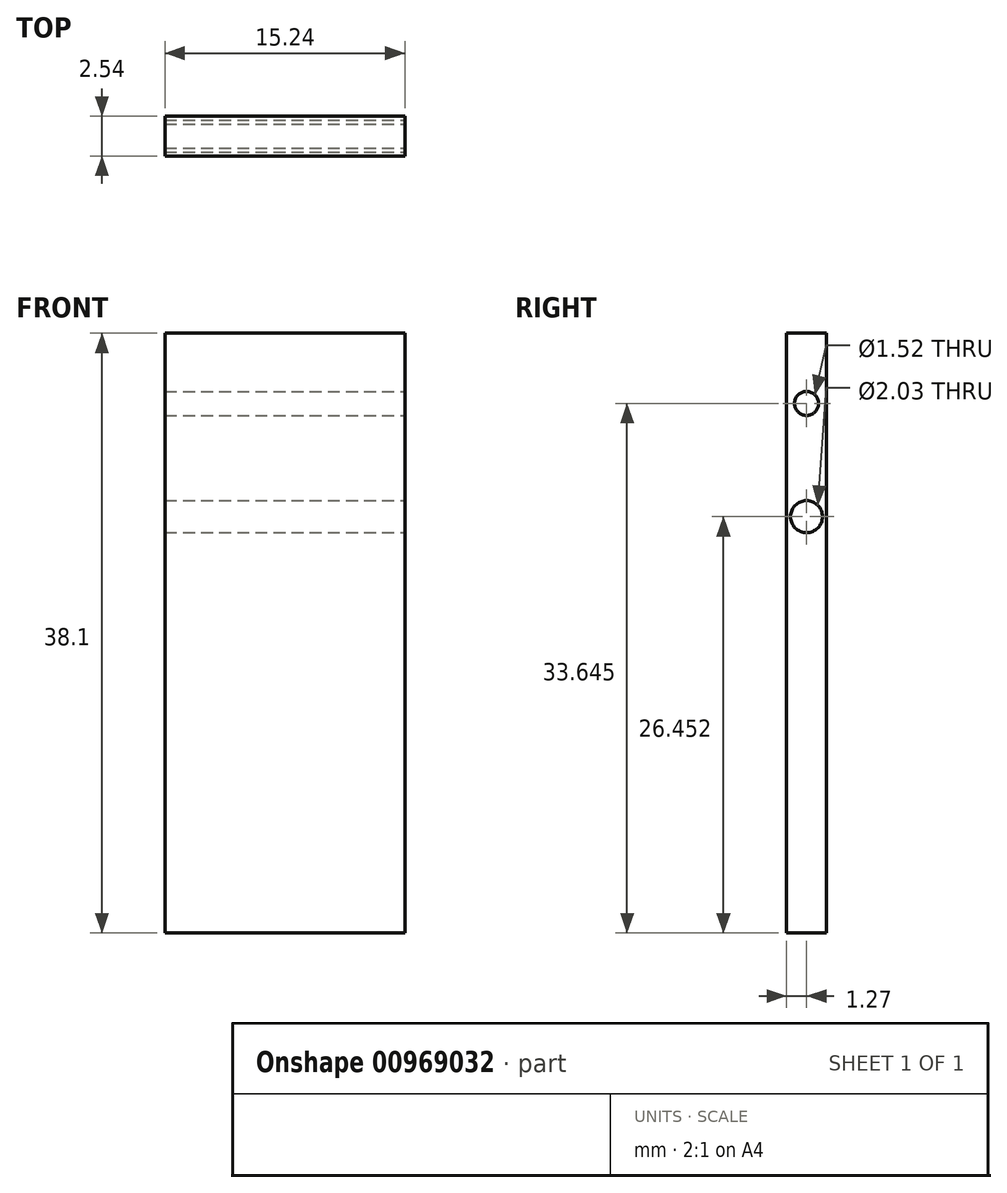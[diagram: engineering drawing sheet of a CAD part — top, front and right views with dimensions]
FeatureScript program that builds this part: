
annotation { "Feature Type Name" : "Feature", "Feature Type Description" : "" }
export const myFeature = defineFeature(function(context is Context, id is Id, definition is map)
    precondition{}
    {
        {
            var Q0;
            Q0=qCreatedBy(makeId("Front.planeOp"),FACE);
            var sketch = newSketch(context, id + "F0", { "sketchPlane" : qUnion([Q0])});
            skLineSegment(sketch, "E0.bottom", {"start": v(7.62, 19.05) * mm, "end": v(-7.62, 19.05) * mm});
            skLineSegment(sketch, "E0.top", {"start": v(7.62, -19.05) * mm, "end": v(-7.62, -19.05) * mm});
            skLineSegment(sketch, "E0.left", {"start": v(7.62, 19.05) * mm, "end": v(7.62, -19.05) * mm});
            skLineSegment(sketch, "E0.right", {"start": v(-7.62, 19.05) * mm, "end": v(-7.62, -19.05) * mm});
            skPoint(sketch, "E0.middle", {"position": v(0, 0) * mm});
            skSolve(sketch);
        }
        {
            var Q0;
            Q0=makeQuery(id+"F0.imprint","IMPRINT",FACE,{"disambiguationData":[TD([[makeQuery(id+"F0.imprint","IMPRINT",EDGE,{"derivedFrom":sQuery(id+"F0.wireOp",EDGE,"E0.bottom")}),1.0]])]});
            extrude(context, id + "F1", {"entities" : qUnion([Q0]), "endBound" : BoundingType.SYMMETRIC, "depth" : 2.54 * mm, "offsetDistance" : 25.4 * mm});
        }
        {
            var Q0;
            Q0=qCreatedBy(makeId("Right.planeOp"),FACE);
            var sketch = newSketch(context, id + "F2", { "sketchPlane" : qUnion([Q0])});
            skCircle(sketch, "E1", {"center": v(0, 17.73) * mm, "radius": 0.81 * mm});
            skSolve(sketch);
        }
        {
            var Q0;
            Q0=sQuery(id+"F2.wireOp",EDGE,"E1");
            extrude(context, id + "F3", {"bodyType" : ToolBodyType.SURFACE, "surfaceEntities" : qUnion([Q0]), "endBound" : BoundingType.SYMMETRIC, "depth" : 17.78 * mm, "offsetDistance" : 25.4 * mm});
        }
        {
            var Q0;
            Q0=makeQuery(id+"F1.opExtrude","SWEPT_FACE",FACE,{"disambiguationData":[OSD([sQuery(id+"F0.wireOp",EDGE,"E0.left")])]});
            var sketch = newSketch(context, id + "F4", { "sketchPlane" : qUnion([Q0])});
            skCircle(sketch, "E2", {"center": v(0, 14.6) * mm, "radius": 0.85 * mm});
            skSolve(sketch);
        }
        {
            var Q0;
            Q0=sQuery(id+"F4.wireOp",VERTEX,"E2.center");
            var Q1;
            Q1=makeQuery(id+"F1.opExtrude","SWEPT_BODY",BODY,{"disambiguationData":[OSD([sQuery(id+"F0.wireOp",EDGE,"E0.bottom"),sQuery(id+"F0.wireOp",EDGE,"E0.top"),sQuery(id+"F0.wireOp",EDGE,"E0.left"),sQuery(id+"F0.wireOp",EDGE,"E0.right")])]});
            hole(context, id + "F5", {"style" : HoleStyle.SIMPLE, "endStyle" : HoleEndStyle.THROUGH, "holeDiameter" : 1.52 * mm, "majorDiameter" : 6.35 * mm, "isTappedThrough" : true, "tappedDepth" : 12.7 * mm, "tapClearance" : 3, "locations" : qUnion([Q0]), "scope" : qUnion([Q1])});
        }
        {
            var Q0;
            Q0=makeQuery(id+"F1.opExtrude","SWEPT_FACE",FACE,{"disambiguationData":[OSD([sQuery(id+"F0.wireOp",EDGE,"E0.left")])]});
            var sketch = newSketch(context, id + "F6", { "sketchPlane" : qUnion([Q0])});
            skCircle(sketch, "E3", {"center": v(0, 7.4) * mm, "radius": 1.02 * mm});
            skSolve(sketch);
        }
        {
            var Q0;
            Q0=makeQuery(id+"F6.imprint","IMPRINT",FACE,{"disambiguationData":[TD([[makeQuery(id+"F6.imprint","IMPRINT",EDGE,{"derivedFrom":sQuery(id+"F6.wireOp",EDGE,"E3")}),1.0]])]});
            extrude(context, id + "F7", {"entities" : qUnion([Q0]), "operationType" : NewBodyOperationType.REMOVE, "endBound" : BoundingType.THROUGH_ALL, "oppositeDirection" : true, "depth" : 25.4 * mm, "offsetDistance" : 25.4 * mm});
        }
    });
